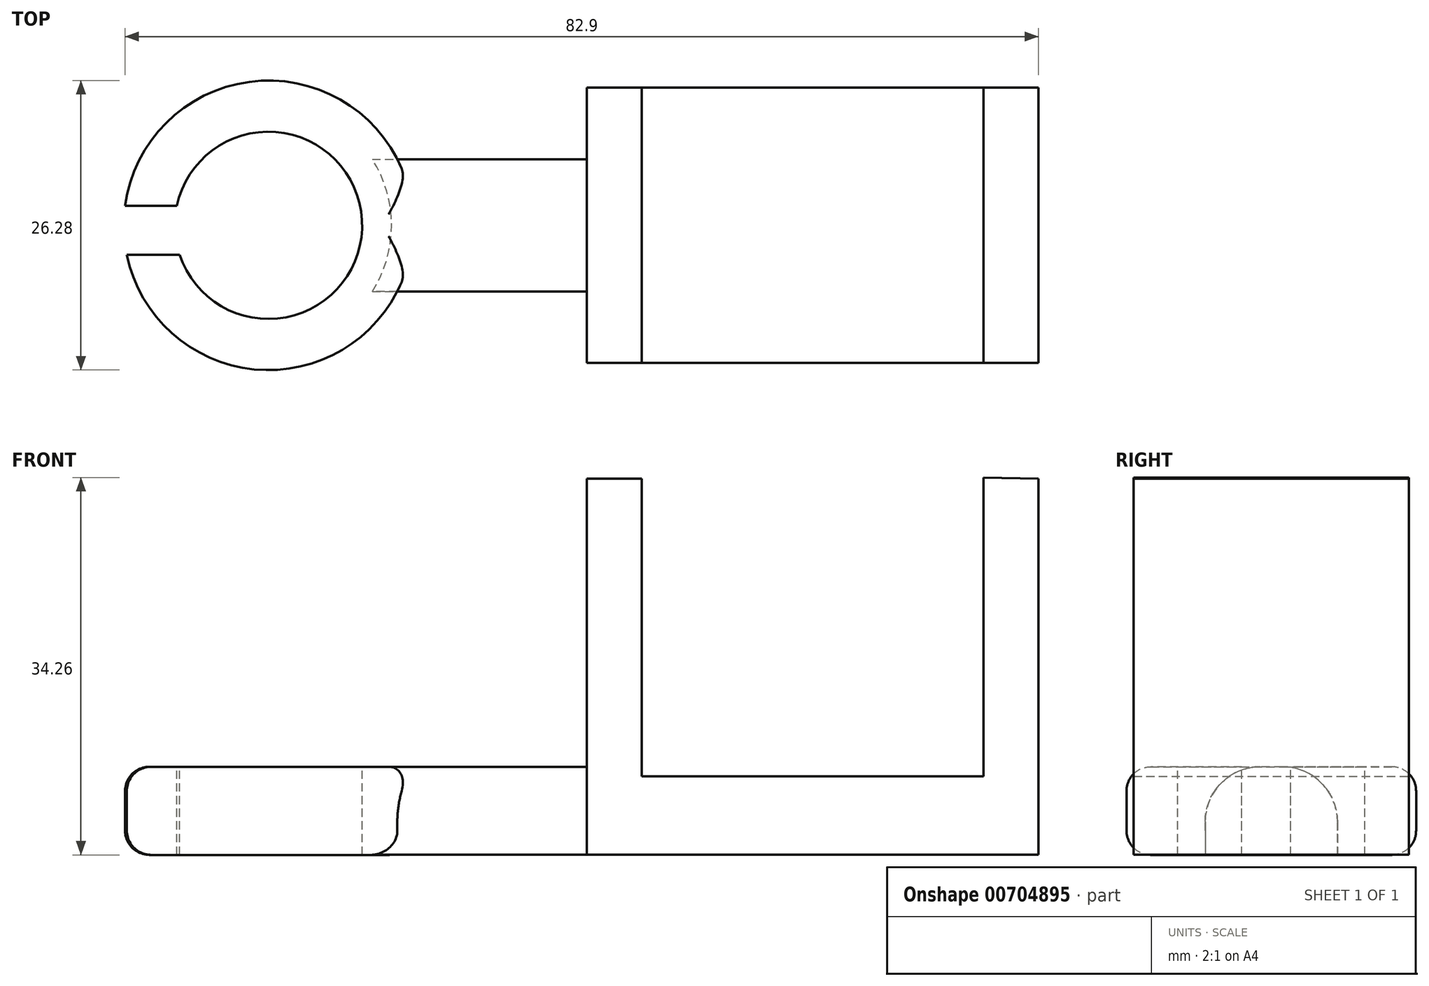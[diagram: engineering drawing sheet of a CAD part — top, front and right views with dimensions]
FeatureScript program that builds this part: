
annotation { "Feature Type Name" : "Feature", "Feature Type Description" : "" }
export const myFeature = defineFeature(function(context is Context, id is Id, definition is map)
    precondition{}
    {
        {
            var Q0;
            Q0=qCreatedBy(makeId("Front.planeOp"),FACE);
            var sketch = newSketch(context, id + "F0", { "sketchPlane" : qUnion([Q0])});
            skLineSegment(sketch, "E0", {"start": v(-15.92, 22) * mm, "end": v(-15.92, 0) * mm});
            skLineSegment(sketch, "E1", {"start": v(-15.92, 0) * mm, "end": v(15.08, 0) * mm});
            skLineSegment(sketch, "E2", {"start": v(15.08, 0) * mm, "end": v(15.08, 22.12) * mm});
            skLineSegment(sketch, "E3", {"start": v(-15.92, 22) * mm, "end": v(-20.92, 22) * mm});
            skLineSegment(sketch, "E4", {"start": v(-20.92, 22) * mm, "end": v(-20.92, -7.12) * mm});
            skLineSegment(sketch, "E5", {"start": v(-20.92, -7.12) * mm, "end": v(20.08, -7.12) * mm});
            skLineSegment(sketch, "E6", {"start": v(20.08, -7.12) * mm, "end": v(20.08, 22) * mm});
            skLineSegment(sketch, "E7", {"start": v(20.08, 22) * mm, "end": v(15.08, 22.12) * mm});
            skSolve(sketch);
        }
        {
            var Q0;
            Q0 = qSketchRegion(id + "F0", true);
            extrude(context, id + "F1", {"entities" : qUnion([Q0]), "depth" : 25 * mm, "offsetDistance" : 25 * mm});
        }
        {
            var Q0;
            Q0=makeQuery(id+"F1.opExtrude","SWEPT_FACE",FACE,{"disambiguationData":[OSD([sQuery(id+"F0.wireOp",EDGE,"E4")])]});
            var sketch = newSketch(context, id + "F2", { "sketchPlane" : qUnion([Q0])});
            skLineSegment(sketch, "E8.bottom", {"start": v(6.5, 0.86) * mm, "end": v(18.5, 0.86) * mm});
            skLineSegment(sketch, "E8.top", {"start": v(6.5, -7.14) * mm, "end": v(18.5, -7.14) * mm});
            skLineSegment(sketch, "E8.left", {"start": v(6.5, 0.86) * mm, "end": v(6.5, -7.14) * mm});
            skLineSegment(sketch, "E8.right", {"start": v(18.5, 0.86) * mm, "end": v(18.5, -7.14) * mm});
            skSolve(sketch);
        }
        {
            var Q0;
            Q0=makeQuery(id+"F2.imprint","IMPRINT",FACE,{"disambiguationData":[TD([[makeQuery(id+"F2.imprint","IMPRINT",EDGE,{"derivedFrom":sQuery(id+"F2.wireOp",EDGE,"E8.bottom")}),-1.0]])]});
            extrude(context, id + "F3", {"entities" : qUnion([Q0]), "operationType" : NewBodyOperationType.ADD, "depth" : 20 * mm, "offsetDistance" : 25 * mm});
        }
        {
            var Q0;
            Q0=makeQuery(id+"F3.opExtrude","SWEPT_FACE",FACE,{"disambiguationData":[OSD([sQuery(id+"F2.wireOp",EDGE,"E8.bottom")])]});
            var sketch = newSketch(context, id + "F4", { "sketchPlane" : qUnion([Q0])});
            skCircle(sketch, "E9", {"center": v(-49.8, -12.5) * mm, "radius": 13.14 * mm});
            skPoint(sketch, "E10", {"position": v(-40.92, -12.5) * mm});
            skSolve(sketch);
        }
        {
            var Q0;
            Q0 = qSketchRegion(id + "F4", true);
            extrude(context, id + "F5", {"entities" : qUnion([Q0]), "operationType" : NewBodyOperationType.ADD, "oppositeDirection" : true, "depth" : 8 * mm, "offsetDistance" : 25 * mm});
        }
        {
            var Q0;
            Q0=makeQuery(id+"F5.boolean.opBoolean","MERGE",FACE,{"derivedFrom":[makeQuery(id+"F3.opExtrude","SWEPT_FACE",FACE,{"disambiguationData":[OSD([sQuery(id+"F2.wireOp",EDGE,"E8.bottom")])]}),makeQuery(id+"F5.opExtrude","CAP_FACE",FACE,{"disambiguationData":[OSD([sQuery(id+"F4.wireOp",EDGE,"E9")])],"isStart":true})]});
            var sketch = newSketch(context, id + "F6", { "sketchPlane" : qUnion([Q0])});
            skCircle(sketch, "E11", {"center": v(-49.8, -12.5) * mm, "radius": 8.5 * mm});
            skSolve(sketch);
        }
        {
            var Q0;
            Q0=makeQuery(id+"F6.imprint","IMPRINT",FACE,{"disambiguationData":[TD([[makeQuery(id+"F6.imprint","IMPRINT",EDGE,{"derivedFrom":sQuery(id+"F6.wireOp",EDGE,"E11")}),1.0]])]});
            extrude(context, id + "F7", {"entities" : qUnion([Q0]), "operationType" : NewBodyOperationType.REMOVE, "oppositeDirection" : true, "depth" : 25 * mm, "offsetDistance" : 25 * mm});
        }
        {
            var Q0;
            Q0=makeQuery(id+"F7.boolean.opBoolean","COPY",EDGE,{"derivedFrom":makeQuery(id+"F7.opExtrude","CAP_EDGE",EDGE,{"disambiguationData":[OSD([sQuery(id+"F6.wireOp",EDGE,"E11")])],"isStart":true})});
            var Q1;
            Q1=makeQuery(id+"F5.opExtrude","CAP_EDGE",EDGE,{"disambiguationData":[OSD([sQuery(id+"F4.wireOp",EDGE,"E9")])],"isStart":true});
            var Q2;
            Q2=makeQuery(id+"F5.opExtrude","CAP_EDGE",EDGE,{"disambiguationData":[OSD([sQuery(id+"F4.wireOp",EDGE,"E9")])],"isStart":false});
            var Q3;
            Q3=makeQuery(id+"F7.boolean.opBoolean","INTERSECT",EDGE,{"derivedFrom":[makeQuery(id+"F5.boolean.opBoolean","MERGE",FACE,{"derivedFrom":[makeQuery(id+"F3.opExtrude","SWEPT_FACE",FACE,{"disambiguationData":[OSD([sQuery(id+"F2.wireOp",EDGE,"E8.top")])]}),makeQuery(id+"F5.opExtrude","CAP_FACE",FACE,{"disambiguationData":[OSD([sQuery(id+"F4.wireOp",EDGE,"E9")])],"isStart":false})]}),makeQuery(id+"F7.opExtrude","SWEPT_FACE",FACE,{"disambiguationData":[OSD([sQuery(id+"F6.wireOp",EDGE,"E11")])]})]});
            fillet(context, id + "F8", {"entities" : qUnion([Q0, Q1, Q2, Q3]), "radius" : 2.2 * mm, "tangentPropagation" : true, "allowEdgeOverflow" : false});
        }
        {
            var Q0;
            Q0=makeQuery(id+"F5.boolean.opBoolean","MERGE",FACE,{"derivedFrom":[makeQuery(id+"F3.opExtrude","SWEPT_FACE",FACE,{"disambiguationData":[OSD([sQuery(id+"F2.wireOp",EDGE,"E8.bottom")])]}),makeQuery(id+"F5.opExtrude","CAP_FACE",FACE,{"disambiguationData":[OSD([sQuery(id+"F4.wireOp",EDGE,"E9")])],"isStart":true})]});
            var sketch = newSketch(context, id + "F9", { "sketchPlane" : qUnion([Q0])});
            skLineSegment(sketch, "E12.bottom", {"start": v(-63.18, -10.73) * mm, "end": v(-57.18, -10.73) * mm});
            skLineSegment(sketch, "E12.top", {"start": v(-63.18, -15.19) * mm, "end": v(-57.18, -15.19) * mm});
            skLineSegment(sketch, "E12.left", {"start": v(-63.18, -10.73) * mm, "end": v(-63.18, -15.19) * mm});
            skLineSegment(sketch, "E12.right", {"start": v(-57.18, -10.73) * mm, "end": v(-57.18, -15.19) * mm});
            skSolve(sketch);
        }
        {
            var Q0;
            Q0 = qSketchRegion(id + "F9", true);
            extrude(context, id + "F10", {"entities" : qUnion([Q0]), "operationType" : NewBodyOperationType.REMOVE, "oppositeDirection" : true, "depth" : 25 * mm, "offsetDistance" : 25 * mm});
        }
        {
            var Q0;
            Q0=makeQuery(id+"F3.opExtrude","SWEPT_EDGE",EDGE,{"disambiguationData":[OSD([sQuery(id+"F2.wireOp",EDGE,"E8.top"),sQuery(id+"F2.wireOp",EDGE,"E8.right")])]});
            var Q1;
            Q1=makeQuery(id+"F3.opExtrude","SWEPT_EDGE",EDGE,{"disambiguationData":[OSD([sQuery(id+"F2.wireOp",EDGE,"E8.bottom"),sQuery(id+"F2.wireOp",EDGE,"E8.right")])]});
            var Q2;
            Q2=makeQuery(id+"F3.opExtrude","SWEPT_EDGE",EDGE,{"disambiguationData":[OSD([sQuery(id+"F2.wireOp",EDGE,"E8.bottom"),sQuery(id+"F2.wireOp",EDGE,"E8.left")])]});
            var Q3;
            Q3=makeQuery(id+"F3.opExtrude","SWEPT_EDGE",EDGE,{"disambiguationData":[OSD([sQuery(id+"F2.wireOp",EDGE,"E8.top"),sQuery(id+"F2.wireOp",EDGE,"E8.left")])]});
            fillet(context, id + "F11", {"entities" : qUnion([Q0, Q1, Q2, Q3]), "radius" : 5 * mm, "tangentPropagation" : true, "allowEdgeOverflow" : false});
        }
        {
            var Q0;
            Q0=makeQuery(id+"F1.opExtrude","SWEPT_FACE",FACE,{"disambiguationData":[OSD([sQuery(id+"F0.wireOp",EDGE,"E3")])]});
            var Q1;
            Q1=makeQuery(id+"F1.opExtrude","SWEPT_FACE",FACE,{"disambiguationData":[OSD([sQuery(id+"F0.wireOp",EDGE,"E7")])]});
            extrude(context, id + "F12", {"entities" : qUnion([Q0, Q1]), "operationType" : NewBodyOperationType.ADD, "depth" : 5 * mm, "offsetDistance" : 25 * mm});
        }
    });
